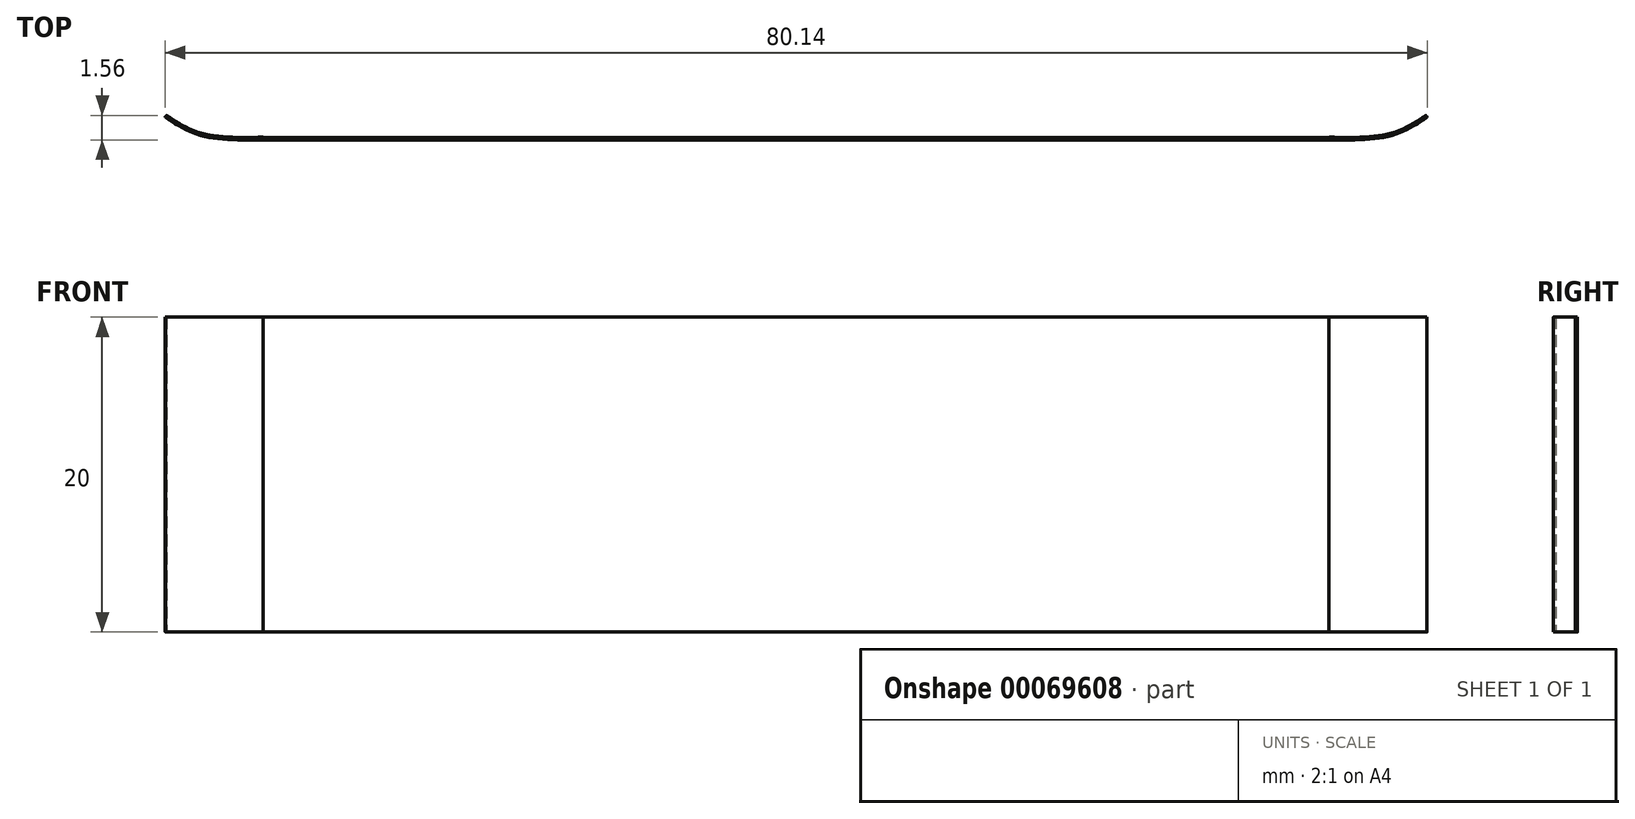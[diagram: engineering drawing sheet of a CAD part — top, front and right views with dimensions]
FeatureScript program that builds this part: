
annotation { "Feature Type Name" : "Feature", "Feature Type Description" : "" }
export const myFeature = defineFeature(function(context is Context, id is Id, definition is map)
    precondition{}
    {
        {
            var Q0;
            Q0=qCreatedBy(makeId("Top.planeOp"),FACE);
            var sketch = newSketch(context, id + "F0", { "sketchPlane" : qUnion([Q0])});
            skLineSegment(sketch, "E0", {"start": v(0, 0) * mm, "end": v(33.85, 0) * mm});
            skFitSpline(sketch, "E1", {"points": [v(33.85, 0) * mm, v(37.77, 0.27) * mm, v(40.06, 1.4) * mm], "startDerivative": vector(7.63, -0.09) * mm, "endDerivative": vector(4.68, 3.02) * mm});
            skFitSpline(sketch, "E2", {"points": [v(40.06, 1.4) * mm, v(40.06, 1.5) * mm, v(39.98, 1.55) * mm, v(39.98, 1.55) * mm], "startDerivative": vector(0.07, 0.2) * mm, "endDerivative": vector(0, -0.01) * mm});
            skFitSpline(sketch, "E3", {"points": [v(39.98, 1.55) * mm, v(37.73, 0.41) * mm, v(33.86, 0.17) * mm], "startDerivative": vector(-4.6, -3) * mm, "endDerivative": vector(-7.54, 0.14) * mm});
            skLineSegment(sketch, "E4", {"start": v(33.86, 0.17) * mm, "end": v(0, 0.14) * mm});
            skLineSegment(sketch, "E5.MirrorCS", {"start": v(-33.86, 0.17) * mm, "end": v(0, 0.14) * mm});
            skLineSegment(sketch, "E6.MirrorCS", {"start": v(0, 0) * mm, "end": v(-33.85, 0) * mm});
            skFitSpline(sketch, "E7.MirrorCS", {"points": [v(-33.85, 0) * mm, v(-37.77, 0.27) * mm, v(-40.06, 1.4) * mm], "startDerivative": vector(-7.63, -0.09) * mm, "endDerivative": vector(-4.68, 3.02) * mm});
            skFitSpline(sketch, "E8.MirrorCS", {"points": [v(-39.98, 1.55) * mm, v(-37.73, 0.41) * mm, v(-33.86, 0.17) * mm], "startDerivative": vector(4.6, -3) * mm, "endDerivative": vector(7.54, 0.14) * mm});
            skFitSpline(sketch, "E9.MirrorCS", {"points": [v(-40.06, 1.4) * mm, v(-40.06, 1.5) * mm, v(-39.98, 1.55) * mm, v(-39.98, 1.55) * mm], "startDerivative": vector(-0.07, 0.2) * mm, "endDerivative": vector(0, -0.01) * mm});
            skSolve(sketch);
        }
        {
            var Q0;
            Q0=makeQuery(id+"F0.imprint","IMPRINT",FACE,{"disambiguationData":[TD([[makeQuery(id+"F0.imprint","IMPRINT",EDGE,{"derivedFrom":sQuery(id+"F0.wireOp",EDGE,"E0")}),1.0]])]});
            extrude(context, id + "F1", {"entities" : qUnion([Q0]), "depth" : 20 * mm});
        }
    });
